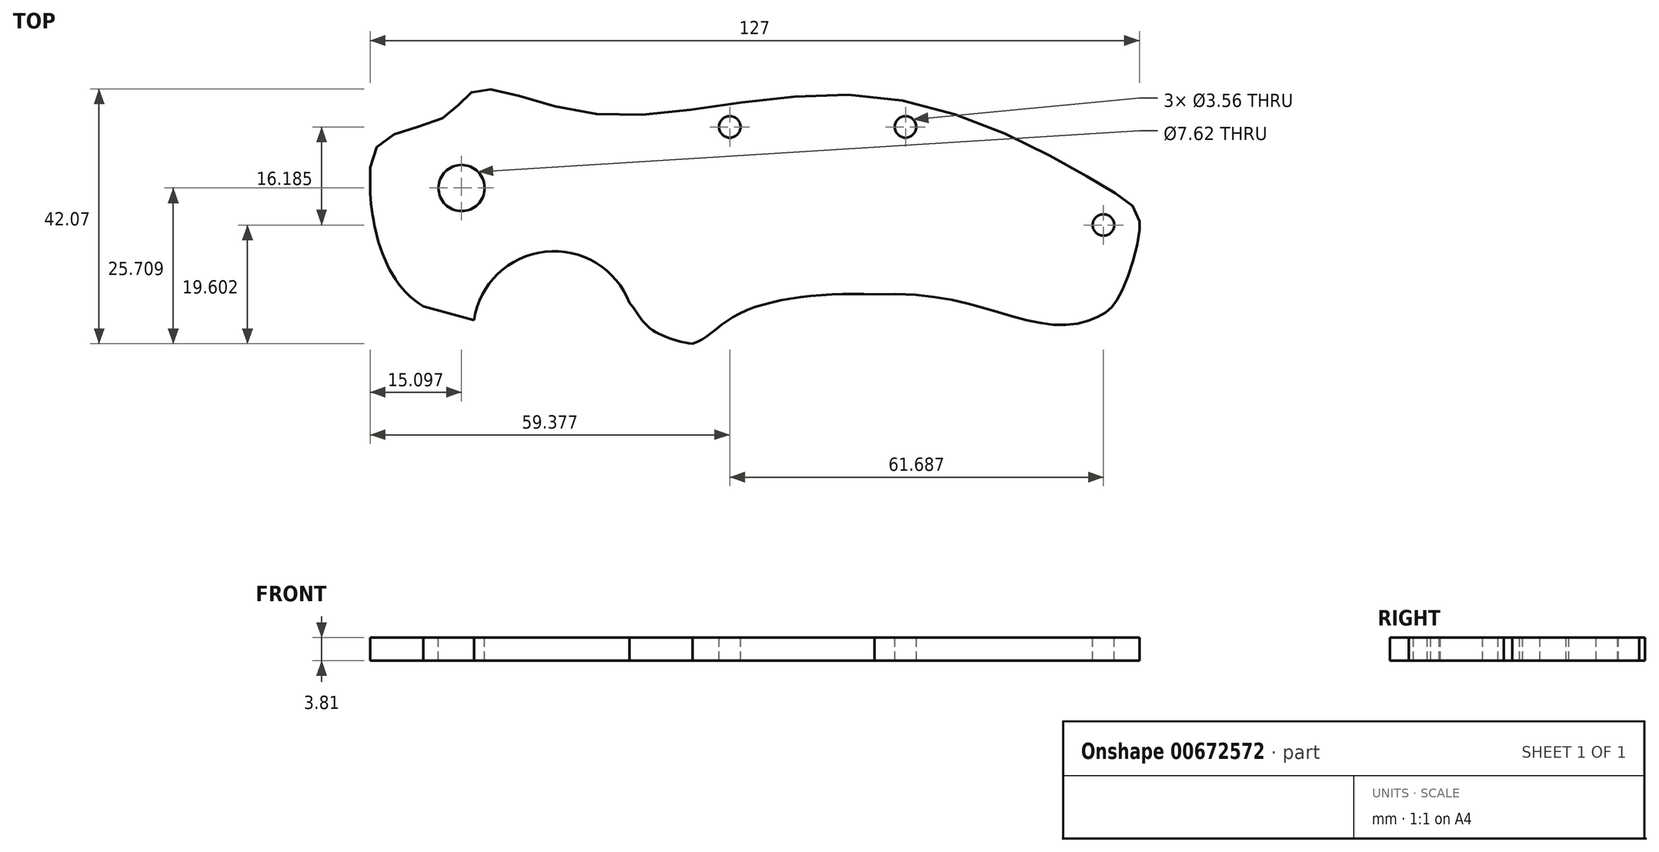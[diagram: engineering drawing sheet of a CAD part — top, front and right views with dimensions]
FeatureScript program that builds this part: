
annotation { "Feature Type Name" : "Feature", "Feature Type Description" : "" }
export const myFeature = defineFeature(function(context is Context, id is Id, definition is map)
    precondition{}
    {
        {
            var Q0;
            Q0=qCreatedBy(makeId("Top.planeOp"),FACE);
            var sketch = newSketch(context, id + "F0", { "sketchPlane" : qUnion([Q0])});
            skLineSegment(sketch, "E0.bottom", {"start": v(63.5, -38.1) * mm, "end": v(-63.5, -38.1) * mm});
            skLineSegment(sketch, "E0.top", {"start": v(63.5, 38.1) * mm, "end": v(-63.5, 38.1) * mm});
            skLineSegment(sketch, "E0.left", {"start": v(63.5, -38.1) * mm, "end": v(63.5, 38.1) * mm});
            skLineSegment(sketch, "E0.right", {"start": v(-63.5, -38.1) * mm, "end": v(-63.5, 38.1) * mm});
            skPoint(sketch, "E0.middle", {"position": v(0, 0) * mm});
            skSolve(sketch);
        }
        {
            var Q0;
            Q0=makeQuery(id+"F0.imprint","IMPRINT",FACE,{"disambiguationData":[TD([[makeQuery(id+"F0.imprint","IMPRINT",EDGE,{"derivedFrom":sQuery(id+"F0.wireOp",EDGE,"E0.bottom")}),-1.0]])]});
            extrude(context, id + "F1", {"entities" : qUnion([Q0]), "depth" : 3.8 * mm, "offsetDistance" : 25.4 * mm});
        }
        {
            var Q0;
            Q0=makeQuery(id+"F1.opExtrude","CAP_FACE",FACE,{"disambiguationData":[OSD([sQuery(id+"F0.wireOp",EDGE,"E0.bottom"),sQuery(id+"F0.wireOp",EDGE,"E0.top"),sQuery(id+"F0.wireOp",EDGE,"E0.left"),sQuery(id+"F0.wireOp",EDGE,"E0.right")])],"isStart":false});
            var sketch = newSketch(context, id + "F2", { "sketchPlane" : qUnion([Q0])});
            skFitSpline(sketch, "E1", {"points": [v(-63.5, 16.64) * mm, v(-61.23, 25.5) * mm, v(-50.85, 29.47) * mm, v(-45.96, 33.74) * mm, v(-26.11, 29.77) * mm, v(21.22, 32.52) * mm, v(59.1, 16.95) * mm, v(63.5, 12.06) * mm, v(60.31, 0) * mm, v(57.56, -3.2) * mm, v(51.46, -5.04) * mm, v(41.07, -3.2) * mm, v(25.5, 0) * mm, v(2.6, -3.51) * mm, v(-6.57, -8.1) * mm, v(-17.56, -5.34) * mm, v(-22.45, 0) * mm, v(-39.24, 0) * mm, v(-44.74, -4.12) * mm, v(-57.26, 0) * mm, v(-63.5, 16.64) * mm]});
            skSolve(sketch);
        }
        {
            var Q0;
            {var subQ5=makeQuery(id+"F1.opExtrude","CAP_EDGE",EDGE,{"disambiguationData":[OSD([sQuery(id+"F0.wireOp",EDGE,"E0.bottom")])],"isStart":false});Q0=makeQuery(id+"F2.imprint","IMPRINT",FACE,{"disambiguationData":[TD([[makeQuery(id+"F2.imprint","IMPRINT",EDGE,{"derivedFrom":subQ5}),-1.0]])]});}
            var Q1;
            {var subQ5=makeQuery(id+"F1.opExtrude","CAP_EDGE",EDGE,{"disambiguationData":[OSD([sQuery(id+"F0.wireOp",EDGE,"E0.top")])],"isStart":false});Q1=makeQuery(id+"F2.imprint","IMPRINT",FACE,{"disambiguationData":[TD([[makeQuery(id+"F2.imprint","IMPRINT",EDGE,{"derivedFrom":subQ5}),1.0]])]});}
            extrude(context, id + "F3", {"entities" : qUnion([Q0, Q1]), "operationType" : NewBodyOperationType.REMOVE, "endBound" : BoundingType.THROUGH_ALL, "oppositeDirection" : true, "depth" : 25.4 * mm, "offsetDistance" : 25.4 * mm});
        }
        {
            var Q0;
            Q0=makeQuery(id+"F1.opExtrude","CAP_FACE",FACE,{"disambiguationData":[OSD([sQuery(id+"F0.wireOp",EDGE,"E0.bottom"),sQuery(id+"F0.wireOp",EDGE,"E0.top"),sQuery(id+"F0.wireOp",EDGE,"E0.left"),sQuery(id+"F0.wireOp",EDGE,"E0.right")])],"isStart":false});
            var sketch = newSketch(context, id + "F4", { "sketchPlane" : qUnion([Q0])});
            skLineSegment(sketch, "E2", {"start": v(-54.7, -1.99) * mm, "end": v(-45.89, -4.38) * mm});
            skCircle(sketch, "E3", {"center": v(-33.13, -6.26) * mm, "radius": 13.38 * mm});
            skEllipse(sketch, "E4", {"center": v(16.34, -12.37) * mm, "majorRadius": 26.48 * mm, "minorRadius": 12.58 * mm, "majorAxis": v(1, 0.13)});
            skSolve(sketch);
        }
        {
            var Q0;
            {var subQ0=sQuery(id+"F4.wireOp",EDGE,"E3");var subQ1=sQuery(id+"F2.wireOp",EDGE,"E1");var subQ2=makeQuery(id+"F3.boolean.opBoolean","COPY",EDGE,{"derivedFrom":makeQuery(id+"F3.opExtrude","CAP_EDGE",EDGE,{"disambiguationData":[OSD([subQ1]),TDD([makeQuery(id+"F2.imprint","IMPRINT",EDGE,{"disambiguationData":[TD([[makeQuery(id+"F2.imprint","INTERSECT",VERTEX,{"disambiguationData":[OD(1.0)],"derivedFrom":[makeQuery(id+"F1.opExtrude","CAP_EDGE",EDGE,{"disambiguationData":[OSD([sQuery(id+"F0.wireOp",EDGE,"E0.right")])],"isStart":false}),subQ1]}),1.0]])],"derivedFrom":subQ1})])],"isStart":true})});var subQ3=makeQuery(id+"F4.imprint","INTERSECT",VERTEX,{"disambiguationData":[OD(0.0)],"derivedFrom":[subQ2,subQ0]});Q0=makeQuery(id+"F4.imprint","IMPRINT",FACE,{"disambiguationData":[TD([[makeQuery(id+"F4.imprint","IMPRINT",EDGE,{"disambiguationData":[TD([[subQ3,1.0]])],"derivedFrom":subQ0}),1.0]])]});}
            var Q1;
            {var subQ0=sQuery(id+"F4.wireOp",EDGE,"E2");var subQ4=sQuery(id+"F4.wireOp",EDGE,"E3");var subQ5=makeQuery(id+"F4.imprint","INTERSECT",VERTEX,{"derivedFrom":[subQ0,subQ4]});Q1=makeQuery(id+"F4.imprint","IMPRINT",FACE,{"disambiguationData":[TD([[makeQuery(id+"F4.imprint","IMPRINT",EDGE,{"disambiguationData":[TD([[subQ5,-1.0]])],"derivedFrom":subQ0}),1.0]])]});}
            var Q2;
            {var subQ0=sQuery(id+"F4.wireOp",EDGE,"E4");var subQ1=sQuery(id+"F2.wireOp",EDGE,"E1");var subQ2=makeQuery(id+"F3.boolean.opBoolean","COPY",EDGE,{"derivedFrom":makeQuery(id+"F3.opExtrude","CAP_EDGE",EDGE,{"disambiguationData":[OSD([subQ1]),TDD([makeQuery(id+"F2.imprint","IMPRINT",EDGE,{"disambiguationData":[TD([[makeQuery(id+"F2.imprint","INTERSECT",VERTEX,{"disambiguationData":[OD(1.0)],"derivedFrom":[makeQuery(id+"F1.opExtrude","CAP_EDGE",EDGE,{"disambiguationData":[OSD([sQuery(id+"F0.wireOp",EDGE,"E0.right")])],"isStart":false}),subQ1]}),1.0]])],"derivedFrom":subQ1})])],"isStart":true})});var subQ3=makeQuery(id+"F4.imprint","INTERSECT",VERTEX,{"disambiguationData":[OD(0.0)],"derivedFrom":[subQ2,subQ0]});Q2=makeQuery(id+"F4.imprint","IMPRINT",FACE,{"disambiguationData":[TD([[makeQuery(id+"F4.imprint","IMPRINT",EDGE,{"disambiguationData":[TD([[subQ3,1.0]])],"derivedFrom":subQ0}),1.0]])]});}
            var Q3;
            {var subQ0=sQuery(id+"F4.wireOp",EDGE,"E2");var subQ4=sQuery(id+"F4.wireOp",EDGE,"E3");var subQ5=makeQuery(id+"F4.imprint","INTERSECT",VERTEX,{"derivedFrom":[subQ0,subQ4]});Q3=makeQuery(id+"F4.imprint","IMPRINT",FACE,{"disambiguationData":[TD([[makeQuery(id+"F4.imprint","IMPRINT",EDGE,{"disambiguationData":[TD([[subQ5,1.0]])],"derivedFrom":subQ0}),-1.0]])]});}
            extrude(context, id + "F5", {"entities" : qUnion([Q0, Q1, Q2, Q3]), "operationType" : NewBodyOperationType.REMOVE, "endBound" : BoundingType.THROUGH_ALL, "oppositeDirection" : true, "depth" : 25.4 * mm, "offsetDistance" : 25.4 * mm});
        }
        {
            var Q0;
            {var subQ1=sQuery(id+"F0.wireOp",EDGE,"E0.right");var subQ3=sQuery(id+"F0.wireOp",EDGE,"E0.left");Q0=makeQuery(id+"F5.boolean.opBoolean","SPLIT",FACE,{"disambiguationData":[TD([makeQuery(id+"F1.opExtrude","SWEPT_FACE",FACE,{"disambiguationData":[OSD([subQ3])]})])],"derivedFrom":makeQuery(id+"F1.opExtrude","CAP_FACE",FACE,{"disambiguationData":[OSD([sQuery(id+"F0.wireOp",EDGE,"E0.bottom"),sQuery(id+"F0.wireOp",EDGE,"E0.top"),subQ3,subQ1])],"isStart":false})});}
            var sketch = newSketch(context, id + "F6", { "sketchPlane" : qUnion([Q0])});
            skFitSpline(sketch, "E5", {"points": [v(-23.23, 2.75) * mm, v(-17.4, -5.48) * mm, v(-10.24, -8.15) * mm, v(-2.58, -3.2) * mm, v(19.77, 0) * mm, v(43.26, -3.83) * mm, v(55.8, -10.53) * mm, v(42.96, -25.2) * mm, v(-17.87, -22.76) * mm, v(-23.23, 2.75) * mm]});
            skSolve(sketch);
        }
        {
            var Q0;
            {var subQ0=sQuery(id+"F6.wireOp",EDGE,"E5");var subQ1=sQuery(id+"F0.wireOp",EDGE,"E0.right");var subQ2=sQuery(id+"F0.wireOp",EDGE,"E0.left");var subQ3=sQuery(id+"F2.wireOp",EDGE,"E1");var subQ4=makeQuery(id+"F2.imprint","IMPRINT",EDGE,{"disambiguationData":[TD([[makeQuery(id+"F2.imprint","INTERSECT",VERTEX,{"disambiguationData":[OD(1.0)],"derivedFrom":[makeQuery(id+"F1.opExtrude","CAP_EDGE",EDGE,{"disambiguationData":[OSD([subQ1])],"isStart":false}),subQ3]}),1.0]])],"derivedFrom":subQ3});var subQ6=makeQuery(id+"F3.boolean.opBoolean","COPY",EDGE,{"derivedFrom":makeQuery(id+"F3.opExtrude","CAP_EDGE",EDGE,{"disambiguationData":[OSD([subQ3]),TDD([subQ4])],"isStart":true})});var subQ8=makeQuery(id+"F5.boolean.opBoolean","SPLIT",EDGE,{"disambiguationData":[TD([makeQuery(id+"F1.opExtrude","SWEPT_FACE",FACE,{"disambiguationData":[OSD([subQ2])]})])],"derivedFrom":subQ6});var subQ9=makeQuery(id+"F6.imprint","INTERSECT",VERTEX,{"disambiguationData":[OD(2.0)],"derivedFrom":[subQ8,subQ0]});Q0=makeQuery(id+"F6.imprint","IMPRINT",FACE,{"disambiguationData":[TD([[makeQuery(id+"F6.imprint","IMPRINT",EDGE,{"disambiguationData":[TD([[subQ9,-1.0]])],"derivedFrom":subQ0}),-1.0]])]});}
            extrude(context, id + "F7", {"entities" : qUnion([Q0]), "operationType" : NewBodyOperationType.REMOVE, "endBound" : BoundingType.THROUGH_ALL, "oppositeDirection" : true, "depth" : 25.4 * mm, "offsetDistance" : 25.4 * mm});
        }
        {
            var Q0;
            {var subQ1=sQuery(id+"F0.wireOp",EDGE,"E0.right");var subQ3=sQuery(id+"F0.wireOp",EDGE,"E0.left");Q0=makeQuery(id+"F5.boolean.opBoolean","SPLIT",FACE,{"disambiguationData":[TD([makeQuery(id+"F1.opExtrude","SWEPT_FACE",FACE,{"disambiguationData":[OSD([subQ3])]})])],"derivedFrom":makeQuery(id+"F1.opExtrude","CAP_FACE",FACE,{"disambiguationData":[OSD([sQuery(id+"F0.wireOp",EDGE,"E0.bottom"),sQuery(id+"F0.wireOp",EDGE,"E0.top"),subQ3,subQ1])],"isStart":false})});}
            var sketch = newSketch(context, id + "F8", { "sketchPlane" : qUnion([Q0])});
            skLineSegment(sketch, "E6", {"start": v(-17.57, -8.87) * mm, "end": v(3.3, -6.1) * mm});
            skLineSegment(sketch, "E7", {"start": v(3.3, -6.1) * mm, "end": v(-7.14, -16.53) * mm});
            skLineSegment(sketch, "E8", {"start": v(-7.14, -16.53) * mm, "end": v(-17.57, -8.87) * mm});
            skSolve(sketch);
        }
        {
            var Q0;
            {var subQ0=sQuery(id+"F8.wireOp",EDGE,"E6");var subQ11=sQuery(id+"F6.wireOp",EDGE,"E5");var subQ14=makeQuery(id+"F7.boolean.opBoolean","COPY",EDGE,{"derivedFrom":makeQuery(id+"F7.opExtrude","CAP_EDGE",EDGE,{"disambiguationData":[OSD([subQ11])],"isStart":true})});var subQ15=makeQuery(id+"F8.imprint","INTERSECT",VERTEX,{"derivedFrom":[subQ14,subQ0]});Q0=makeQuery(id+"F8.imprint","IMPRINT",FACE,{"disambiguationData":[TD([[makeQuery(id+"F8.imprint","IMPRINT",EDGE,{"disambiguationData":[TD([[subQ15,1.0]])],"derivedFrom":subQ0}),-1.0]])]});}
            extrude(context, id + "F9", {"entities" : qUnion([Q0]), "operationType" : NewBodyOperationType.REMOVE, "endBound" : BoundingType.THROUGH_ALL, "oppositeDirection" : true, "depth" : 25.4 * mm, "offsetDistance" : 25.4 * mm});
        }
        {
            var Q0;
            {var subQ1=sQuery(id+"F0.wireOp",EDGE,"E0.right");var subQ3=sQuery(id+"F0.wireOp",EDGE,"E0.left");Q0=makeQuery(id+"F5.boolean.opBoolean","SPLIT",FACE,{"disambiguationData":[TD([makeQuery(id+"F1.opExtrude","SWEPT_FACE",FACE,{"disambiguationData":[OSD([subQ3])]})])],"derivedFrom":makeQuery(id+"F1.opExtrude","CAP_FACE",FACE,{"disambiguationData":[OSD([sQuery(id+"F0.wireOp",EDGE,"E0.bottom"),sQuery(id+"F0.wireOp",EDGE,"E0.top"),subQ3,subQ1])],"isStart":false})});}
            var sketch = newSketch(context, id + "F10", { "sketchPlane" : qUnion([Q0])});
            skLineSegment(sketch, "E9", {"start": v(-47.84, -5.25) * mm, "end": v(-44.37, -2.7) * mm});
            skLineSegment(sketch, "E10", {"start": v(-44.37, -2.7) * mm, "end": v(-44.37, -5.15) * mm});
            skLineSegment(sketch, "E11", {"start": v(-44.37, -5.15) * mm, "end": v(-47.84, -5.25) * mm});
            skSolve(sketch);
        }
        {
            var Q0;
            {var subQ1=sQuery(id+"F10.wireOp",EDGE,"E10");Q0=makeQuery(id+"F10.imprint","IMPRINT",FACE,{"disambiguationData":[TD([[makeQuery(id+"F10.imprint","IMPRINT",EDGE,{"derivedFrom":subQ1}),-1.0]])]});}
            extrude(context, id + "F11", {"entities" : qUnion([Q0]), "operationType" : NewBodyOperationType.REMOVE, "endBound" : BoundingType.THROUGH_ALL, "oppositeDirection" : true, "depth" : 25.4 * mm, "offsetDistance" : 25.4 * mm});
        }
        {
            var Q0;
            {var subQ1=sQuery(id+"F0.wireOp",EDGE,"E0.right");var subQ3=sQuery(id+"F0.wireOp",EDGE,"E0.left");Q0=makeQuery(id+"F5.boolean.opBoolean","SPLIT",FACE,{"disambiguationData":[TD([makeQuery(id+"F1.opExtrude","SWEPT_FACE",FACE,{"disambiguationData":[OSD([subQ3])]})])],"derivedFrom":makeQuery(id+"F1.opExtrude","CAP_FACE",FACE,{"disambiguationData":[OSD([sQuery(id+"F0.wireOp",EDGE,"E0.bottom"),sQuery(id+"F0.wireOp",EDGE,"E0.top"),subQ3,subQ1])],"isStart":false})});}
            var sketch = newSketch(context, id + "F12", { "sketchPlane" : qUnion([Q0])});
            skCircle(sketch, "E12", {"center": v(-48.4, 17.56) * mm, "radius": 3.81 * mm});
            skCircle(sketch, "E13", {"center": v(-4.12, 27.64) * mm, "radius": 1.78 * mm});
            skCircle(sketch, "E14", {"center": v(24.89, 27.64) * mm, "radius": 1.78 * mm});
            skCircle(sketch, "E15", {"center": v(57.56, 11.45) * mm, "radius": 1.78 * mm});
            skSolve(sketch);
        }
        {
            var Q0;
            Q0=makeQuery(id+"F12.imprint","IMPRINT",FACE,{"disambiguationData":[TD([[makeQuery(id+"F12.imprint","IMPRINT",EDGE,{"derivedFrom":sQuery(id+"F12.wireOp",EDGE,"E12")}),1.0]])]});
            var Q1;
            Q1=makeQuery(id+"F12.imprint","IMPRINT",FACE,{"disambiguationData":[TD([[makeQuery(id+"F12.imprint","IMPRINT",EDGE,{"derivedFrom":sQuery(id+"F12.wireOp",EDGE,"E13")}),1.0]])]});
            var Q2;
            Q2=makeQuery(id+"F12.imprint","IMPRINT",FACE,{"disambiguationData":[TD([[makeQuery(id+"F12.imprint","IMPRINT",EDGE,{"derivedFrom":sQuery(id+"F12.wireOp",EDGE,"E14")}),1.0]])]});
            var Q3;
            Q3=makeQuery(id+"F12.imprint","IMPRINT",FACE,{"disambiguationData":[TD([[makeQuery(id+"F12.imprint","IMPRINT",EDGE,{"derivedFrom":sQuery(id+"F12.wireOp",EDGE,"E15")}),1.0]])]});
            var Q4;
            Q4=sQuery(id+"F12.wireOp",EDGE,"E12");
            var Q5;
            Q5=sQuery(id+"F12.wireOp",EDGE,"E13");
            var Q6;
            Q6=sQuery(id+"F12.wireOp",EDGE,"E14");
            var Q7;
            Q7=sQuery(id+"F12.wireOp",EDGE,"E15");
            extrude(context, id + "F13", {"entities" : qUnion([Q0, Q1, Q2, Q3]), "operationType" : NewBodyOperationType.REMOVE, "surfaceEntities" : qUnion([Q4, Q5, Q6, Q7]), "endBound" : BoundingType.THROUGH_ALL, "oppositeDirection" : true, "depth" : 25.4 * mm, "offsetDistance" : 25.4 * mm});
        }
    });
